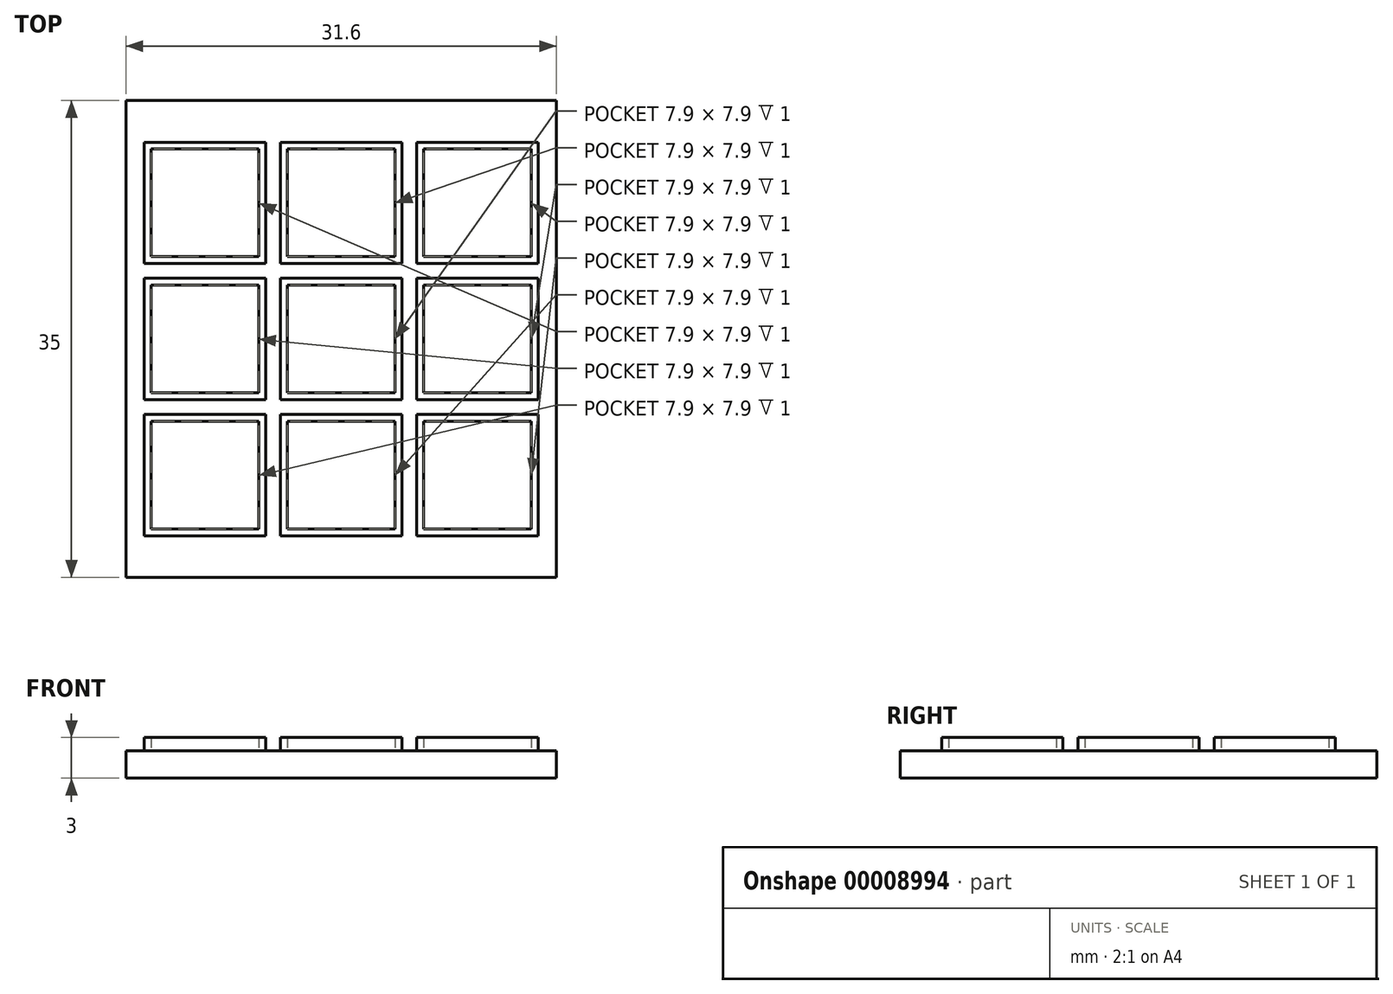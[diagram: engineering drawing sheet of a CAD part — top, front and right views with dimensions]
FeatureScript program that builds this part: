
annotation { "Feature Type Name" : "Feature", "Feature Type Description" : "" }
export const myFeature = defineFeature(function(context is Context, id is Id, definition is map)
    precondition{}
    {
        {
            var Q0;
            Q0=qCreatedBy(makeId("Top.planeOp"),FACE);
            var sketch = newSketch(context, id + "F0", { "sketchPlane" : qUnion([Q0])});
            skLineSegment(sketch, "E0.bottom", {"start": v(0, 0) * mm, "end": v(31.6, 0) * mm});
            skLineSegment(sketch, "E0.top", {"start": v(0, -35) * mm, "end": v(31.6, -35) * mm});
            skLineSegment(sketch, "E0.left", {"start": v(0, 0) * mm, "end": v(0, -35) * mm});
            skLineSegment(sketch, "E0.right", {"start": v(31.6, 0) * mm, "end": v(31.6, -35) * mm});
            skSolve(sketch);
        }
        {
            var Q0;
            Q0 = qSketchRegion(id + "F0", true);
            extrude(context, id + "F1", {"entities" : qUnion([Q0]), "depth" : 2 * mm});
        }
        {
            var Q0;
            Q0=makeQuery(id+"F1.opExtrude","CAP_FACE",FACE,{"disambiguationData":[OSD([sQuery(id+"F0.wireOp",EDGE,"E0.bottom"),sQuery(id+"F0.wireOp",EDGE,"E0.top"),sQuery(id+"F0.wireOp",EDGE,"E0.left"),sQuery(id+"F0.wireOp",EDGE,"E0.right")])],"isStart":false});
            var sketch = newSketch(context, id + "F2", { "sketchPlane" : qUnion([Q0])});
            skLineSegment(sketch, "E1.bottom", {"start": v(0, -35) * mm, "end": v(31.6, -35) * mm});
            skLineSegment(sketch, "E1.top", {"start": v(0, 0) * mm, "end": v(31.6, 0) * mm});
            skLineSegment(sketch, "E1.left", {"start": v(0, -35) * mm, "end": v(0, 0) * mm});
            skLineSegment(sketch, "E1.right", {"start": v(31.6, -35) * mm, "end": v(31.6, 0) * mm});
            skLineSegment(sketch, "E2", {"start": v(15.8, 0) * mm, "end": v(15.8, -35) * mm, "construction": true});
            skLineSegment(sketch, "E3.rect.bottom", {"start": v(20.25, -21.95) * mm, "end": v(11.35, -21.95) * mm});
            skLineSegment(sketch, "E3.rect.top", {"start": v(20.25, -13.05) * mm, "end": v(11.35, -13.05) * mm});
            skLineSegment(sketch, "E3.rect.left", {"start": v(20.25, -21.95) * mm, "end": v(20.25, -13.05) * mm});
            skLineSegment(sketch, "E3.rect.right", {"start": v(11.35, -21.95) * mm, "end": v(11.35, -13.05) * mm});
            skPoint(sketch, "E3.rect.middle", {"position": v(15.8, -17.5) * mm});
            skLineSegment(sketch, "E4.rect.bottom", {"start": v(19.75, -21.45) * mm, "end": v(11.85, -21.45) * mm});
            skLineSegment(sketch, "E4.rect.top", {"start": v(19.75, -13.55) * mm, "end": v(11.85, -13.55) * mm});
            skLineSegment(sketch, "E4.rect.left", {"start": v(19.75, -21.45) * mm, "end": v(19.75, -13.55) * mm});
            skLineSegment(sketch, "E4.rect.right", {"start": v(11.85, -21.45) * mm, "end": v(11.85, -13.55) * mm});
            skLineSegment(sketch, "E5.0.1.0", {"start": v(11.35, -11.95) * mm, "end": v(11.35, -3.05) * mm});
            skLineSegment(sketch, "E5.0.1.1", {"start": v(11.85, -11.45) * mm, "end": v(11.85, -3.55) * mm});
            skLineSegment(sketch, "E5.0.1.2", {"start": v(19.75, -11.45) * mm, "end": v(11.85, -11.45) * mm});
            skLineSegment(sketch, "E5.0.1.3", {"start": v(20.25, -11.95) * mm, "end": v(11.35, -11.95) * mm});
            skLineSegment(sketch, "E5.0.1.4", {"start": v(20.25, -11.95) * mm, "end": v(20.25, -3.05) * mm});
            skLineSegment(sketch, "E5.0.1.5", {"start": v(20.25, -3.05) * mm, "end": v(11.35, -3.05) * mm});
            skLineSegment(sketch, "E5.0.1.6", {"start": v(19.75, -3.55) * mm, "end": v(11.85, -3.55) * mm});
            skLineSegment(sketch, "E5.0.1.7", {"start": v(19.75, -11.45) * mm, "end": v(19.75, -3.55) * mm});
            skLineSegment(sketch, "E5.1.0.0", {"start": v(21.35, -21.95) * mm, "end": v(21.35, -13.05) * mm});
            skLineSegment(sketch, "E5.1.0.1", {"start": v(21.85, -21.45) * mm, "end": v(21.85, -13.55) * mm});
            skLineSegment(sketch, "E5.1.0.2", {"start": v(29.75, -21.45) * mm, "end": v(21.85, -21.45) * mm});
            skLineSegment(sketch, "E5.1.0.3", {"start": v(30.25, -21.95) * mm, "end": v(21.35, -21.95) * mm});
            skLineSegment(sketch, "E5.1.0.4", {"start": v(30.25, -21.95) * mm, "end": v(30.25, -13.05) * mm});
            skLineSegment(sketch, "E5.1.0.5", {"start": v(30.25, -13.05) * mm, "end": v(21.35, -13.05) * mm});
            skLineSegment(sketch, "E5.1.0.6", {"start": v(29.75, -13.55) * mm, "end": v(21.85, -13.55) * mm});
            skLineSegment(sketch, "E5.1.0.7", {"start": v(29.75, -21.45) * mm, "end": v(29.75, -13.55) * mm});
            skLineSegment(sketch, "E5.1.1.0", {"start": v(21.35, -11.95) * mm, "end": v(21.35, -3.05) * mm});
            skLineSegment(sketch, "E5.1.1.1", {"start": v(21.85, -11.45) * mm, "end": v(21.85, -3.55) * mm});
            skLineSegment(sketch, "E5.1.1.2", {"start": v(29.75, -11.45) * mm, "end": v(21.85, -11.45) * mm});
            skLineSegment(sketch, "E5.1.1.3", {"start": v(30.25, -11.95) * mm, "end": v(21.35, -11.95) * mm});
            skLineSegment(sketch, "E5.1.1.4", {"start": v(30.25, -11.95) * mm, "end": v(30.25, -3.05) * mm});
            skLineSegment(sketch, "E5.1.1.5", {"start": v(30.25, -3.05) * mm, "end": v(21.35, -3.05) * mm});
            skLineSegment(sketch, "E5.1.1.6", {"start": v(29.75, -3.55) * mm, "end": v(21.85, -3.55) * mm});
            skLineSegment(sketch, "E5.1.1.7", {"start": v(29.75, -11.45) * mm, "end": v(29.75, -3.55) * mm});
            skLineSegment(sketch, "E5.direction1", {"start": v(11.35, -21.95) * mm, "end": v(21.35, -21.95) * mm, "construction": true});
            skLineSegment(sketch, "E5.direction2", {"start": v(11.35, -21.95) * mm, "end": v(11.35, -11.95) * mm, "construction": true});
            skLineSegment(sketch, "E6.0.1.0", {"start": v(30.25, -31.95) * mm, "end": v(30.25, -23.05) * mm});
            skLineSegment(sketch, "E6.0.1.1", {"start": v(29.75, -31.45) * mm, "end": v(29.75, -23.55) * mm});
            skLineSegment(sketch, "E6.0.1.2", {"start": v(29.75, -23.55) * mm, "end": v(21.85, -23.55) * mm});
            skLineSegment(sketch, "E6.0.1.3", {"start": v(30.25, -23.05) * mm, "end": v(21.35, -23.05) * mm});
            skLineSegment(sketch, "E6.0.1.4", {"start": v(20.25, -31.95) * mm, "end": v(20.25, -23.05) * mm});
            skLineSegment(sketch, "E6.0.1.5", {"start": v(21.35, -31.95) * mm, "end": v(21.35, -23.05) * mm});
            skLineSegment(sketch, "E6.0.1.6", {"start": v(21.85, -31.45) * mm, "end": v(21.85, -23.55) * mm});
            skLineSegment(sketch, "E6.0.1.7", {"start": v(20.25, -23.05) * mm, "end": v(11.35, -23.05) * mm});
            skLineSegment(sketch, "E6.0.1.8", {"start": v(19.75, -23.55) * mm, "end": v(11.85, -23.55) * mm});
            skLineSegment(sketch, "E6.0.1.9", {"start": v(11.85, -31.45) * mm, "end": v(11.85, -23.55) * mm});
            skLineSegment(sketch, "E6.0.1.10", {"start": v(11.35, -31.95) * mm, "end": v(11.35, -23.05) * mm});
            skLineSegment(sketch, "E6.0.1.11", {"start": v(19.75, -31.45) * mm, "end": v(11.85, -31.45) * mm});
            skLineSegment(sketch, "E6.0.1.12", {"start": v(20.25, -31.95) * mm, "end": v(11.35, -31.95) * mm});
            skLineSegment(sketch, "E6.0.1.13", {"start": v(30.25, -31.95) * mm, "end": v(21.35, -31.95) * mm});
            skLineSegment(sketch, "E6.0.1.14", {"start": v(29.75, -31.45) * mm, "end": v(21.85, -31.45) * mm});
            skLineSegment(sketch, "E6.direction1", {"start": v(30.25, -21.95) * mm, "end": v(55.25, -21.95) * mm, "construction": true});
            skLineSegment(sketch, "E6.direction2", {"start": v(30.25, -21.95) * mm, "end": v(30.25, -31.95) * mm, "construction": true});
            skLineSegment(sketch, "E7.1.0.0", {"start": v(10.25, -11.95) * mm, "end": v(1.35, -11.95) * mm});
            skLineSegment(sketch, "E7.1.0.1", {"start": v(10.25, -13.05) * mm, "end": v(1.35, -13.05) * mm});
            skLineSegment(sketch, "E7.1.0.2", {"start": v(9.75, -11.45) * mm, "end": v(9.75, -3.55) * mm});
            skLineSegment(sketch, "E7.1.0.3", {"start": v(5.8, 0) * mm, "end": v(5.8, -35) * mm, "construction": true});
            skLineSegment(sketch, "E7.1.0.4", {"start": v(10.25, -21.95) * mm, "end": v(1.35, -21.95) * mm});
            skPoint(sketch, "E7.1.0.5", {"position": v(5.8, -17.5) * mm});
            skLineSegment(sketch, "E7.1.0.6", {"start": v(9.75, -11.45) * mm, "end": v(1.85, -11.45) * mm});
            skLineSegment(sketch, "E7.1.0.7", {"start": v(1.85, -11.45) * mm, "end": v(1.85, -3.55) * mm});
            skLineSegment(sketch, "E7.1.0.8", {"start": v(1.35, -11.95) * mm, "end": v(1.35, -3.05) * mm});
            skLineSegment(sketch, "E7.1.0.9", {"start": v(10.25, -31.95) * mm, "end": v(1.35, -31.95) * mm});
            skLineSegment(sketch, "E7.1.0.10", {"start": v(10.25, -21.95) * mm, "end": v(10.25, -13.05) * mm});
            skLineSegment(sketch, "E7.1.0.11", {"start": v(9.75, -3.55) * mm, "end": v(1.85, -3.55) * mm});
            skLineSegment(sketch, "E7.1.0.12", {"start": v(1.35, -21.95) * mm, "end": v(1.35, -13.05) * mm});
            skLineSegment(sketch, "E7.1.0.13", {"start": v(9.75, -21.45) * mm, "end": v(1.85, -21.45) * mm});
            skLineSegment(sketch, "E7.1.0.14", {"start": v(9.75, -13.55) * mm, "end": v(1.85, -13.55) * mm});
            skLineSegment(sketch, "E7.1.0.15", {"start": v(9.75, -21.45) * mm, "end": v(9.75, -13.55) * mm});
            skLineSegment(sketch, "E7.1.0.16", {"start": v(1.85, -21.45) * mm, "end": v(1.85, -13.55) * mm});
            skLineSegment(sketch, "E7.1.0.17", {"start": v(9.75, -23.55) * mm, "end": v(1.85, -23.55) * mm});
            skLineSegment(sketch, "E7.1.0.18", {"start": v(9.75, -31.45) * mm, "end": v(1.85, -31.45) * mm});
            skLineSegment(sketch, "E7.1.0.19", {"start": v(10.25, -3.05) * mm, "end": v(1.35, -3.05) * mm});
            skLineSegment(sketch, "E7.1.0.20", {"start": v(1.85, -31.45) * mm, "end": v(1.85, -23.55) * mm});
            skLineSegment(sketch, "E7.1.0.21", {"start": v(10.25, -11.95) * mm, "end": v(10.25, -3.05) * mm});
            skLineSegment(sketch, "E7.1.0.22", {"start": v(1.35, -31.95) * mm, "end": v(1.35, -23.05) * mm});
            skLineSegment(sketch, "E7.1.0.23", {"start": v(10.25, -31.95) * mm, "end": v(10.25, -23.05) * mm});
            skPoint(sketch, "E7.1.0.24", {"position": v(5.8, -17.5) * mm});
            skLineSegment(sketch, "E7.1.0.25", {"start": v(10.25, -23.05) * mm, "end": v(1.35, -23.05) * mm});
            skLineSegment(sketch, "E7.1.0.26", {"start": v(1.35, -21.95) * mm, "end": v(1.35, -11.95) * mm, "construction": true});
            skLineSegment(sketch, "E7.direction1", {"start": v(11.35, -11.95) * mm, "end": v(1.35, -11.95) * mm, "construction": true});
            skLineSegment(sketch, "E8", {"start": v(9.75, -23.55) * mm, "end": v(9.75, -31.45) * mm});
            skLineSegment(sketch, "E9", {"start": v(19.75, -31.45) * mm, "end": v(19.75, -23.55) * mm});
            skSolve(sketch);
        }
        {
            var Q0;
            Q0=makeQuery(id+"F2.imprint","IMPRINT",FACE,{"disambiguationData":[TD([[makeQuery(id+"F2.imprint","IMPRINT",EDGE,{"derivedFrom":sQuery(id+"F2.wireOp",EDGE,"E7.1.0.9")}),-1.0]])]});
            var Q1;
            Q1=makeQuery(id+"F2.imprint","IMPRINT",FACE,{"disambiguationData":[TD([[makeQuery(id+"F2.imprint","IMPRINT",EDGE,{"derivedFrom":sQuery(id+"F2.wireOp",EDGE,"E6.0.1.4")}),1.0]])]});
            var Q2;
            Q2=makeQuery(id+"F2.imprint","IMPRINT",FACE,{"disambiguationData":[TD([[makeQuery(id+"F2.imprint","IMPRINT",EDGE,{"derivedFrom":sQuery(id+"F2.wireOp",EDGE,"E6.0.1.0")}),1.0]])]});
            var Q3;
            Q3=makeQuery(id+"F2.imprint","IMPRINT",FACE,{"disambiguationData":[TD([[makeQuery(id+"F2.imprint","IMPRINT",EDGE,{"derivedFrom":sQuery(id+"F2.wireOp",EDGE,"E5.1.0.0")}),-1.0]])]});
            var Q4;
            Q4=makeQuery(id+"F2.imprint","IMPRINT",FACE,{"disambiguationData":[TD([[makeQuery(id+"F2.imprint","IMPRINT",EDGE,{"derivedFrom":sQuery(id+"F2.wireOp",EDGE,"E3.rect.bottom")}),-1.0]])]});
            var Q5;
            Q5=makeQuery(id+"F2.imprint","IMPRINT",FACE,{"disambiguationData":[TD([[makeQuery(id+"F2.imprint","IMPRINT",EDGE,{"derivedFrom":sQuery(id+"F2.wireOp",EDGE,"E7.1.0.1")}),1.0]])]});
            var Q6;
            Q6=makeQuery(id+"F2.imprint","IMPRINT",FACE,{"disambiguationData":[TD([[makeQuery(id+"F2.imprint","IMPRINT",EDGE,{"derivedFrom":sQuery(id+"F2.wireOp",EDGE,"E7.1.0.0")}),-1.0]])]});
            var Q7;
            Q7=makeQuery(id+"F2.imprint","IMPRINT",FACE,{"disambiguationData":[TD([[makeQuery(id+"F2.imprint","IMPRINT",EDGE,{"derivedFrom":sQuery(id+"F2.wireOp",EDGE,"E5.0.1.0")}),-1.0]])]});
            var Q8;
            Q8=makeQuery(id+"F2.imprint","IMPRINT",FACE,{"disambiguationData":[TD([[makeQuery(id+"F2.imprint","IMPRINT",EDGE,{"derivedFrom":sQuery(id+"F2.wireOp",EDGE,"E5.1.1.0")}),-1.0]])]});
            extrude(context, id + "F3", {"entities" : qUnion([Q0, Q1, Q2, Q3, Q4, Q5, Q6, Q7, Q8]), "operationType" : NewBodyOperationType.ADD, "depth" : 1 * mm});
        }
    });
